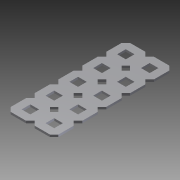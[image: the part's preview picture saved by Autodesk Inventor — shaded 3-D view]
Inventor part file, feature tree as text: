
AUTODESK INVENTOR PART (.ipt)
format: ipt  version: 2014 SP1 (Build 180222100, 222)  size: 599,552 bytes
history: native  units: in
note: dims shown in document units (in); Inventor stores cm internally (conversion verified against a paired STEP export)
features: extrude x2, sketch x2, other x1, imported_body x1
ambient origin geometry x8: Origin, YZ Plane, XZ Plane, XY Plane, X Axis, Y Axis, Z Axis, Center Point
bodies: Body1 (feature_tree)
feature tree (6):
  parser-record x1  (decoder bookkeeping rows leaked as tree rows — omitted from the tree; the rows remain in map.json)
  imported_body  "Base1"
  extrude  "Extrusion1"  Depth=1.0in TaperAngle=0.0deg
  extrude  "Extrusion2"  Depth=2.5in
  sketch  "Sketch1"  dims[d0=1.5in d1=1.0in d2=0.0in]
  sketch  "Sketch2"  dims[d3=1.0in d4=0.0in d5=2.5in]
